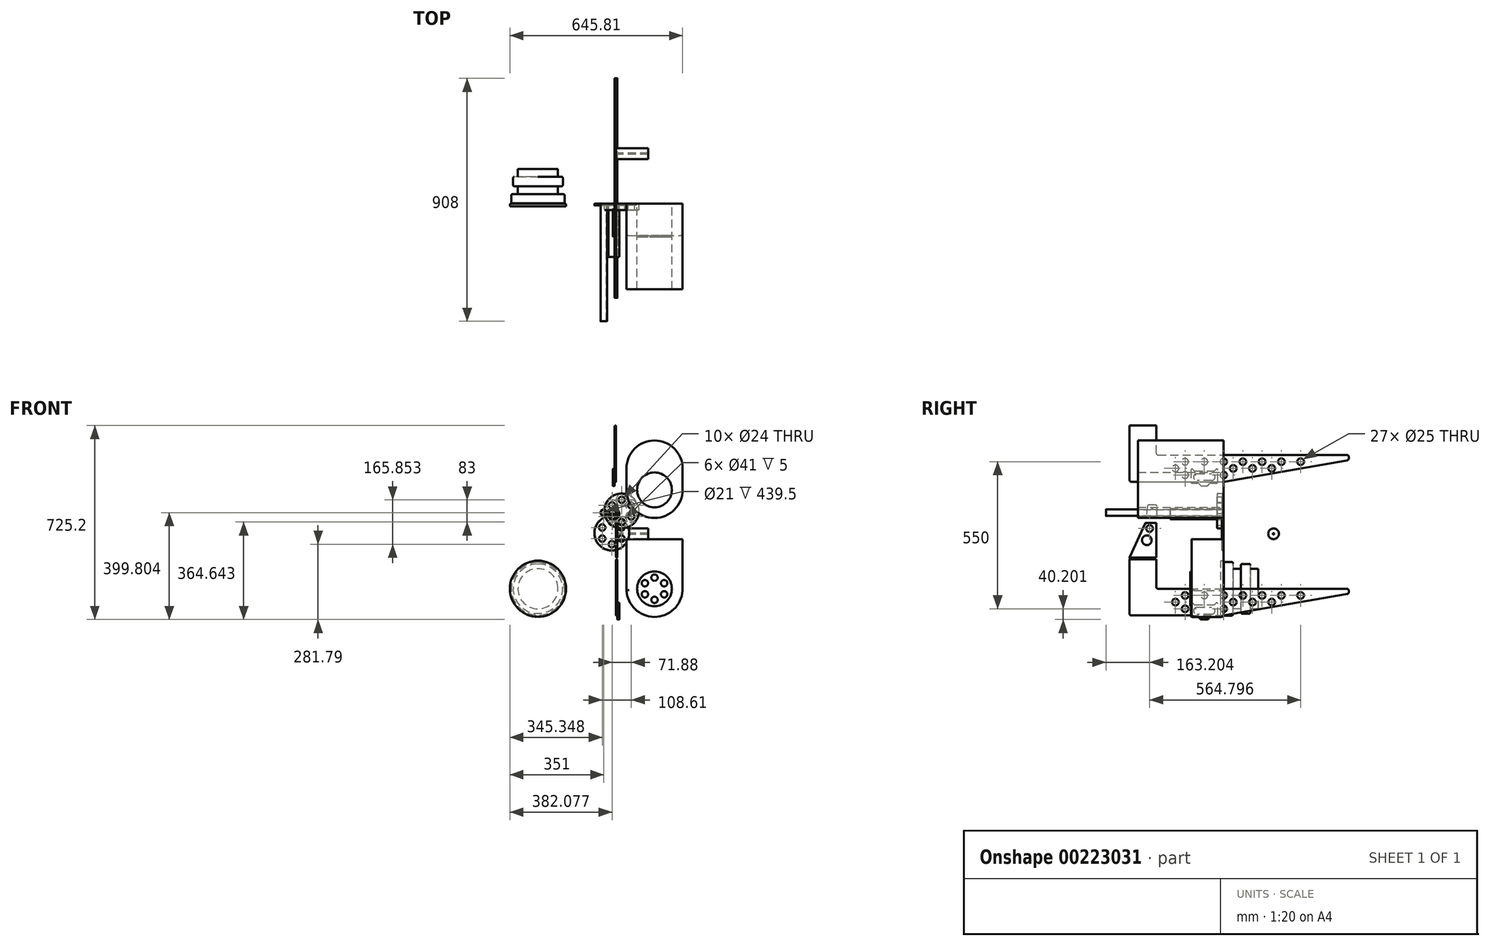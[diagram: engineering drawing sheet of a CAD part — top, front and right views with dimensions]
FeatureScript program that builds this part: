
annotation { "Feature Type Name" : "Feature", "Feature Type Description" : "" }
export const myFeature = defineFeature(function(context is Context, id is Id, definition is map)
    precondition{}
    {
        {
            var Q0;
            Q0=qCreatedBy(makeId("Front.planeOp"),FACE);
            var sketch = newSketch(context, id + "F0", { "sketchPlane" : qUnion([Q0])});
            skCircle(sketch, "E0", {"center": v(-46.15, 24.2) * mm, "radius": 10.5 * mm});
            skCircle(sketch, "E1", {"center": v(-46.15, 24.2) * mm, "radius": 12 * mm});
            skSolve(sketch);
        }
        {
            assignVariable(context, id + "F1", {"name" : "frontbarrel", "anyValue" : 440});
        }
        {
            var Q0;
            Q0=makeQuery(id+"F0.imprint","IMPRINT",FACE,{"disambiguationData":[TD([[makeQuery(id+"F0.imprint","IMPRINT",EDGE,{"derivedFrom":sQuery(id+"F0.wireOp",EDGE,"E0")}),-1.0]])]});
            extrude(context, id + "F2", {"entities" : qUnion([Q0]), "depth" : (getVariable(context, 'frontbarrel')) * mm});
        }
        {
            var Q0;
            Q0=qCreatedBy(makeId("Front.planeOp"),FACE);
            var sketch = newSketch(context, id + "F3", { "sketchPlane" : qUnion([Q0])});
            skCircle(sketch, "E2", {"center": v(-7.96, 19.9) * mm, "radius": 20.5 * mm});
            skCircle(sketch, "E3", {"center": v(-7.96, 19.9) * mm, "radius": 19 * mm});
            skCircle(sketch, "E4", {"center": v(-7.96, 19.9) * mm, "radius": 12 * mm, "construction": true});
            skPoint(sketch, "E5", {"position": v(-46.15, 24.2) * mm});
            skPoint(sketch, "E6", {"position": v(-46.38, 36.2) * mm});
            skCircle(sketch, "E7", {"center": v(-46.15, 24.2) * mm, "radius": 12 * mm, "construction": true});
            skSolve(sketch);
        }
        {
            var Q0;
            Q0=makeQuery(id+"F3.imprint","IMPRINT",FACE,{"disambiguationData":[TD([[makeQuery(id+"F3.imprint","IMPRINT",EDGE,{"derivedFrom":sQuery(id+"F3.wireOp",EDGE,"E2")}),1.0]])]});
            extrude(context, id + "F4", {"entities" : qUnion([Q0]), "depth" : 200 * mm});
        }
        {
            var Q0;
            Q0=qCreatedBy(makeId("Front.planeOp"),FACE);
            var sketch = newSketch(context, id + "F5", { "sketchPlane" : qUnion([Q0])});
            skPoint(sketch, "E8", {"position": v(-7.96, 19.9) * mm});
            skPoint(sketch, "E9", {"position": v(-24.67, 31.78) * mm});
            skPoint(sketch, "E10", {"position": v(-46.15, 24.2) * mm});
            skPoint(sketch, "E11", {"position": v(-43.79, 35.97) * mm});
            skCircle(sketch, "E12", {"center": v(-7.96, 19.9) * mm, "radius": 20.5 * mm, "construction": true});
            skCircle(sketch, "E13", {"center": v(-46.15, 24.2) * mm, "radius": 12 * mm, "construction": true});
            skCircle(sketch, "E14", {"center": v(-15.86, -52.31) * mm, "radius": 65 * mm});
            skCircle(sketch, "E15", {"center": v(-15.86, -52.31) * mm, "radius": 62 * mm, "construction": true});
            skPoint(sketch, "E16", {"position": v(-15.86, 9.69) * mm});
            skCircle(sketch, "E17", {"center": v(-15.86, -10.81) * mm, "radius": 20.5 * mm, "construction": true});
            skCircle(sketch, "E18.1.0", {"center": v(-51.8, -31.56) * mm, "radius": 20.5 * mm, "construction": true});
            skCircle(sketch, "E18.2.0", {"center": v(-51.8, -73.06) * mm, "radius": 20.5 * mm, "construction": true});
            skCircle(sketch, "E18.3.0", {"center": v(-15.86, -93.81) * mm, "radius": 20.5 * mm, "construction": true});
            skCircle(sketch, "E18.4.0", {"center": v(20.08, -73.06) * mm, "radius": 20.5 * mm, "construction": true});
            skCircle(sketch, "E18.5.0", {"center": v(20.08, -31.56) * mm, "radius": 20.5 * mm, "construction": true});
            skCircle(sketch, "E19", {"center": v(-15.86, -10.81) * mm, "radius": 12 * mm});
            skCircle(sketch, "E20.1.0", {"center": v(-51.8, -31.56) * mm, "radius": 12 * mm});
            skCircle(sketch, "E20.2.0", {"center": v(-51.8, -73.06) * mm, "radius": 12 * mm});
            skCircle(sketch, "E20.3.0", {"center": v(-15.86, -93.81) * mm, "radius": 12 * mm});
            skCircle(sketch, "E20.4.0", {"center": v(20.08, -73.06) * mm, "radius": 12 * mm});
            skCircle(sketch, "E20.5.0", {"center": v(20.08, -31.56) * mm, "radius": 12 * mm});
            skSolve(sketch);
        }
        {
            var Q0;
            Q0=makeQuery(id+"F5.imprint","IMPRINT",FACE,{"disambiguationData":[TD([[makeQuery(id+"F5.imprint","IMPRINT",EDGE,{"derivedFrom":sQuery(id+"F5.wireOp",EDGE,"E14")}),1.0]])]});
            extrude(context, id + "F6", {"entities" : qUnion([Q0]), "depth" : 7 * mm});
        }
        {
            var Q0;
            Q0=qCreatedBy(makeId("Front.planeOp"),FACE);
            var sketch = newSketch(context, id + "F7", { "sketchPlane" : qUnion([Q0])});
            skCircle(sketch, "E21", {"center": v(20.87, 30.54) * mm, "radius": 65 * mm});
            skPoint(sketch, "E22", {"position": v(-15.86, -52.31) * mm});
            skPoint(sketch, "E23", {"position": v(27.16, -3.59) * mm});
            skCircle(sketch, "E24", {"center": v(-15.86, -52.31) * mm, "radius": 65 * mm, "construction": true});
            skPoint(sketch, "E25", {"position": v(20.87, 95.54) * mm});
            skPoint(sketch, "E26", {"position": v(-15.86, -93.81) * mm});
            skLineSegment(sketch, "E27", {"start": v(-15.86, -93.81) * mm, "end": v(-15.86, -52.31) * mm, "construction": true});
            skLineSegment(sketch, "E28", {"start": v(20.87, 30.54) * mm, "end": v(20.87, 72.04) * mm, "construction": true});
            skPoint(sketch, "E29", {"position": v(-7.96, 40.4) * mm});
            skPoint(sketch, "E30", {"position": v(-7.96, 19.9) * mm});
            skCircle(sketch, "E31", {"center": v(-7.96, 19.9) * mm, "radius": 20.5 * mm, "construction": true});
            skPoint(sketch, "E32", {"position": v(-46.15, 24.2) * mm});
            skPoint(sketch, "E33", {"position": v(-46.15, 36.2) * mm});
            skCircle(sketch, "E34", {"center": v(-46.15, 24.2) * mm, "radius": 12 * mm, "construction": true});
            skCircle(sketch, "E35", {"center": v(20.87, 72.04) * mm, "radius": 12 * mm});
            skCircle(sketch, "E36.1.0", {"center": v(-15.07, 51.3) * mm, "radius": 12 * mm});
            skCircle(sketch, "E36.2.0", {"center": v(-15.07, 9.8) * mm, "radius": 12 * mm});
            skCircle(sketch, "E36.3.0", {"center": v(20.87, -10.96) * mm, "radius": 12 * mm});
            skCircle(sketch, "E36.4.0", {"center": v(56.8, 9.8) * mm, "radius": 12 * mm});
            skCircle(sketch, "E36.5.0", {"center": v(56.8, 51.3) * mm, "radius": 12 * mm});
            skSolve(sketch);
        }
        {
            var Q0;
            Q0=makeQuery(id+"F7.imprint","IMPRINT",FACE,{"disambiguationData":[TD([[makeQuery(id+"F7.imprint","IMPRINT",EDGE,{"derivedFrom":sQuery(id+"F7.wireOp",EDGE,"E21")}),1.0]])]});
            extrude(context, id + "F8", {"entities" : qUnion([Q0]), "depth" : 24 * mm});
        }
        {
            var Q0;
            Q0=makeQuery(id+"F8.opExtrude","CAP_FACE",FACE,{"disambiguationData":[OSD([sQuery(id+"F7.wireOp",EDGE,"E21"),sQuery(id+"F7.wireOp",EDGE,"E35"),sQuery(id+"F7.wireOp",EDGE,"E36.1.0"),sQuery(id+"F7.wireOp",EDGE,"E36.2.0"),sQuery(id+"F7.wireOp",EDGE,"E36.3.0"),sQuery(id+"F7.wireOp",EDGE,"E36.4.0"),sQuery(id+"F7.wireOp",EDGE,"E36.5.0")])],"isStart":true});
            var sketch = newSketch(context, id + "F9", { "sketchPlane" : qUnion([Q0])});
            skPoint(sketch, "E37", {"position": v(-20.87, 72.04) * mm});
            skPoint(sketch, "E38", {"position": v(7.96, 19.9) * mm});
            skPoint(sketch, "E39", {"position": v(7.96, 40.4) * mm});
            skCircle(sketch, "E40", {"center": v(7.96, 19.9) * mm, "radius": 20.5 * mm, "construction": true});
            skCircle(sketch, "E41", {"center": v(-20.87, 72.04) * mm, "radius": 20.5 * mm});
            skPoint(sketch, "E42", {"position": v(-20.87, 30.54) * mm});
            skPoint(sketch, "E43", {"position": v(-23.92, 92.31) * mm});
            skCircle(sketch, "E44.1.0", {"center": v(-56.8, 51.3) * mm, "radius": 20.5 * mm});
            skCircle(sketch, "E44.2.0", {"center": v(-56.8, 9.8) * mm, "radius": 20.5 * mm});
            skCircle(sketch, "E44.3.0", {"center": v(-20.87, -10.96) * mm, "radius": 20.5 * mm});
            skCircle(sketch, "E44.4.0", {"center": v(15.07, 9.8) * mm, "radius": 20.5 * mm});
            skCircle(sketch, "E44.5.0", {"center": v(15.07, 51.3) * mm, "radius": 20.5 * mm});
            skSolve(sketch);
        }
        {
            var Q0;
            Q0=makeQuery(id+"F9.imprint","IMPRINT",FACE,{"disambiguationData":[TD([[makeQuery(id+"F9.imprint","IMPRINT",EDGE,{"derivedFrom":sQuery(id+"F9.wireOp",EDGE,"E41")}),1.0]])]});
            var Q1;
            Q1=makeQuery(id+"F9.imprint","IMPRINT",FACE,{"disambiguationData":[TD([[makeQuery(id+"F9.imprint","IMPRINT",EDGE,{"derivedFrom":sQuery(id+"F9.wireOp",EDGE,"E44.1.0")}),1.0]])]});
            var Q2;
            Q2=makeQuery(id+"F9.imprint","IMPRINT",FACE,{"disambiguationData":[TD([[makeQuery(id+"F9.imprint","IMPRINT",EDGE,{"derivedFrom":sQuery(id+"F9.wireOp",EDGE,"E44.2.0")}),1.0]])]});
            var Q3;
            Q3=makeQuery(id+"F9.imprint","IMPRINT",FACE,{"disambiguationData":[TD([[makeQuery(id+"F9.imprint","IMPRINT",EDGE,{"derivedFrom":sQuery(id+"F9.wireOp",EDGE,"E44.3.0")}),1.0]])]});
            var Q4;
            Q4=makeQuery(id+"F9.imprint","IMPRINT",FACE,{"disambiguationData":[TD([[makeQuery(id+"F9.imprint","IMPRINT",EDGE,{"derivedFrom":sQuery(id+"F9.wireOp",EDGE,"E44.4.0")}),1.0]])]});
            var Q5;
            Q5=makeQuery(id+"F9.imprint","IMPRINT",FACE,{"disambiguationData":[TD([[makeQuery(id+"F9.imprint","IMPRINT",EDGE,{"derivedFrom":sQuery(id+"F9.wireOp",EDGE,"E44.5.0")}),1.0]])]});
            extrude(context, id + "F10", {"entities" : qUnion([Q0, Q1, Q2, Q3, Q4, Q5]), "operationType" : NewBodyOperationType.REMOVE, "oppositeDirection" : true, "depth" : 5 * mm});
        }
        {
            var Q0;
            Q0=makeQuery(id+"F2.opExtrude","CAP_EDGE",EDGE,{"disambiguationData":[OSD([sQuery(id+"F0.wireOp",EDGE,"E1")])],"isStart":false});
            fillet(context, id + "F11", {"entities" : qUnion([Q0]), "radius" : 0.5 * mm, "tangentPropagation" : true, "allowEdgeOverflow" : false});
        }
        {
            var Q0;
            Q0=makeQuery(id+"F2.opExtrude","CAP_EDGE",EDGE,{"disambiguationData":[OSD([sQuery(id+"F0.wireOp",EDGE,"E0")])],"isStart":false});
            fillet(context, id + "F12", {"entities" : qUnion([Q0]), "radius" : 0.5 * mm, "tangentPropagation" : true, "allowEdgeOverflow" : false});
        }
        {
            var Q0;
            Q0=makeQuery(id+"F6.opExtrude","CAP_FACE",FACE,{"disambiguationData":[OSD([sQuery(id+"F5.wireOp",EDGE,"E14"),sQuery(id+"F5.wireOp",EDGE,"E19"),sQuery(id+"F5.wireOp",EDGE,"E20.1.0"),sQuery(id+"F5.wireOp",EDGE,"E20.2.0"),sQuery(id+"F5.wireOp",EDGE,"E20.3.0"),sQuery(id+"F5.wireOp",EDGE,"E20.4.0"),sQuery(id+"F5.wireOp",EDGE,"E20.5.0")])],"isStart":false});
            var Q1;
            Q1=makeQuery(id+"F6.opExtrude","CAP_EDGE",EDGE,{"disambiguationData":[OSD([sQuery(id+"F5.wireOp",EDGE,"E14")])],"isStart":true});
            fillet(context, id + "F13", {"entities" : qUnion([Q0, Q1]), "radius" : 1 * mm, "tangentPropagation" : true, "allowEdgeOverflow" : false});
        }
        {
            var Q0;
            Q0=makeQuery(id+"F8.opExtrude","CAP_EDGE",EDGE,{"disambiguationData":[OSD([sQuery(id+"F7.wireOp",EDGE,"E21")])],"isStart":false});
            var Q1;
            Q1=makeQuery(id+"F8.opExtrude","CAP_EDGE",EDGE,{"disambiguationData":[OSD([sQuery(id+"F7.wireOp",EDGE,"E21")])],"isStart":true});
            fillet(context, id + "F14", {"entities" : qUnion([Q0, Q1]), "radius" : 2 * mm, "tangentPropagation" : true, "allowEdgeOverflow" : false});
        }
        {
            var Q0;
            Q0=qCreatedBy(makeId("Right.planeOp"),FACE);
            var sketch = newSketch(context, id + "F15", { "sketchPlane" : qUnion([Q0])});
            skLineSegment(sketch, "E45", {"start": v(-245, -260.4) * mm, "end": v(461, -260.4) * mm, "construction": true});
            skLineSegment(sketch, "E46", {"start": v(-252, -260.4) * mm, "end": v(468, -260.4) * mm});
            skLineSegment(sketch, "E47", {"start": v(-345, -360.4) * mm, "end": v(-0.6, -360.4) * mm});
            skLineSegment(sketch, "E48", {"start": v(-252, -253.4) * mm, "end": v(-252, -150.4) * mm});
            skLineSegment(sketch, "E49", {"start": v(-252, -150.4) * mm, "end": v(-352, -150.4) * mm});
            skLineSegment(sketch, "E50", {"start": v(-352, -150.4) * mm, "end": v(-352, -360.4) * mm});
            skLineSegment(sketch, "E51", {"start": v(-352, -310.4) * mm, "end": v(239.6, -310.4) * mm, "construction": true});
            skLineSegment(sketch, "E52", {"start": v(-352, -260.4) * mm, "end": v(-352, -353.4) * mm, "construction": true});
            skCircle(sketch, "E53", {"center": v(-180, -310.4) * mm, "radius": 12.5 * mm});
            skCircle(sketch, "E54", {"center": v(-144, -285.4) * mm, "radius": 12.5 * mm});
            skCircle(sketch, "E55", {"center": v(-144, -335.4) * mm, "radius": 12.5 * mm});
            skCircle(sketch, "E56", {"center": v(-72, -285.4) * mm, "radius": 12.5 * mm});
            skCircle(sketch, "E57", {"center": v(0, -285.4) * mm, "radius": 12.5 * mm});
            skCircle(sketch, "E58", {"center": v(0, -335.4) * mm, "radius": 12.5 * mm});
            skCircle(sketch, "E59", {"center": v(36, -310.4) * mm, "radius": 12.5 * mm});
            skCircle(sketch, "E60", {"center": v(72, -285.4) * mm, "radius": 12.5 * mm});
            skCircle(sketch, "E61", {"center": v(108, -310.4) * mm, "radius": 12.5 * mm});
            skCircle(sketch, "E62", {"center": v(144, -285.4) * mm, "radius": 12.5 * mm});
            skCircle(sketch, "E63", {"center": v(216, -285.4) * mm, "radius": 12.5 * mm});
            skCircle(sketch, "E64", {"center": v(180, -310.4) * mm, "radius": 12.5 * mm});
            skCircle(sketch, "E65", {"center": v(288, -285.4) * mm, "radius": 12.5 * mm});
            skLineSegment(sketch, "E66", {"start": v(-72, -380.4) * mm, "end": v(-36, -380.4) * mm, "construction": true});
            skLineSegment(sketch, "E67", {"start": v(-36, -400.4) * mm, "end": v(0, -400.4) * mm, "construction": true});
            skLineSegment(sketch, "E68", {"start": v(0, -380.4) * mm, "end": v(36, -380.4) * mm, "construction": true});
            skLineSegment(sketch, "E69", {"start": v(36, -400.4) * mm, "end": v(72, -400.4) * mm, "construction": true});
            skLineSegment(sketch, "E70", {"start": v(72, -380.4) * mm, "end": v(108, -380.4) * mm, "construction": true});
            skLineSegment(sketch, "E71", {"start": v(108, -400.4) * mm, "end": v(144, -400.4) * mm, "construction": true});
            skLineSegment(sketch, "E72", {"start": v(144, -380.4) * mm, "end": v(180, -380.4) * mm, "construction": true});
            skLineSegment(sketch, "E73", {"start": v(180, -400.4) * mm, "end": v(216, -400.4) * mm, "construction": true});
            skLineSegment(sketch, "E74", {"start": v(-252, -260.4) * mm, "end": v(-252, -310.4) * mm, "construction": true});
            skLineSegment(sketch, "E75", {"start": v(-252, -310.4) * mm, "end": v(-252, -360.4) * mm, "construction": true});
            skPoint(sketch, "E76", {"position": v(-252, -285.4) * mm});
            skPoint(sketch, "E77", {"position": v(-252, -335.4) * mm});
            skLineSegment(sketch, "E78", {"start": v(-72, -400.4) * mm, "end": v(-108, -400.4) * mm, "construction": true});
            skLineSegment(sketch, "E79", {"start": v(-108, -380.4) * mm, "end": v(-144, -380.4) * mm, "construction": true});
            skLineSegment(sketch, "E80", {"start": v(-144, -400.4) * mm, "end": v(-180, -400.4) * mm, "construction": true});
            skLineSegment(sketch, "E81", {"start": v(216, -380.4) * mm, "end": v(252, -380.4) * mm, "construction": true});
            skLineSegment(sketch, "E82", {"start": v(252, -400.4) * mm, "end": v(288, -400.4) * mm, "construction": true});
            skLineSegment(sketch, "E83", {"start": v(-144, -335.4) * mm, "end": v(-144, -360.4) * mm, "construction": true});
            skLineSegment(sketch, "E84", {"start": v(-180, -310.4) * mm, "end": v(-180, -297.9) * mm, "construction": true});
            skLineSegment(sketch, "E85", {"start": v(468, -267.4) * mm, "end": v(468, -273.26) * mm});
            skLineSegment(sketch, "E86", {"start": v(462.2, -280.16) * mm, "end": v(0.6, -360.3) * mm});
            skLineSegment(sketch, "E87", {"start": v(288, -260.4) * mm, "end": v(288, -310.4) * mm, "construction": true});
            skPoint(sketch, "E88.visualSharp", {"position": v(468, -279.15) * mm});
            skArc(sketch, "E88.filletArc", {"start": v(462.2, -280.16) * mm, "mid": v(466.36, -277.77) * mm, "end": v(468, -273.26) * mm});
            skPoint(sketch, "E89.visualSharp", {"position": v(468, -260.4) * mm});
            skArc(sketch, "E89.filletArc", {"start": v(468, -267.4) * mm, "mid": v(465.95, -262.45) * mm, "end": v(461, -260.4) * mm});
            skPoint(sketch, "E90.visualSharp", {"position": v(0, -360.4) * mm});
            skArc(sketch, "E90.filletArc", {"start": v(-0.6, -360.4) * mm, "mid": v(0, -360.37) * mm, "end": v(0.6, -360.3) * mm});
            skLineSegment(sketch, "E91", {"start": v(-144, -272.9) * mm, "end": v(-144, -260.4) * mm, "construction": true});
            skPoint(sketch, "E92.visualSharp", {"position": v(-352, -360.4) * mm});
            skArc(sketch, "E92.filletArc", {"start": v(-352, -353.4) * mm, "mid": v(-349.95, -358.35) * mm, "end": v(-345, -360.4) * mm});
            skPoint(sketch, "E93.newPointB", {"position": v(-352, -260.4) * mm});
            skArc(sketch, "E93.filletArc", {"start": v(-252, -253.4) * mm, "mid": v(-249.95, -258.35) * mm, "end": v(-245, -260.4) * mm});
            skSolve(sketch);
        }
        {
            var Q0;
            Q0=makeQuery(id+"F15.imprint","IMPRINT",FACE,{"disambiguationData":[TD([[makeQuery(id+"F15.imprint","IMPRINT",EDGE,{"derivedFrom":sQuery(id+"F15.wireOp",EDGE,"E47")}),1.0]])]});
            extrude(context, id + "F16", {"entities" : qUnion([Q0]), "depth" : 5 * mm});
        }
        {
            var Q0;
            Q0=makeQuery(id+"F16.opExtrude","CAP_FACE",FACE,{"disambiguationData":[OSD([sQuery(id+"F15.wireOp",EDGE,"E46"),sQuery(id+"F15.wireOp",EDGE,"E47"),sQuery(id+"F15.wireOp",EDGE,"E48"),sQuery(id+"F15.wireOp",EDGE,"E49"),sQuery(id+"F15.wireOp",EDGE,"E50"),sQuery(id+"F15.wireOp",EDGE,"E53"),sQuery(id+"F15.wireOp",EDGE,"E54"),sQuery(id+"F15.wireOp",EDGE,"E55"),sQuery(id+"F15.wireOp",EDGE,"E56"),sQuery(id+"F15.wireOp",EDGE,"E57"),sQuery(id+"F15.wireOp",EDGE,"E58"),sQuery(id+"F15.wireOp",EDGE,"E59"),sQuery(id+"F15.wireOp",EDGE,"E60"),sQuery(id+"F15.wireOp",EDGE,"E61"),sQuery(id+"F15.wireOp",EDGE,"E62"),sQuery(id+"F15.wireOp",EDGE,"E63"),sQuery(id+"F15.wireOp",EDGE,"E64"),sQuery(id+"F15.wireOp",EDGE,"E65"),sQuery(id+"F15.wireOp",EDGE,"E85"),sQuery(id+"F15.wireOp",EDGE,"E86"),sQuery(id+"F15.wireOp",EDGE,"E88.filletArc"),sQuery(id+"F15.wireOp",EDGE,"E89.filletArc"),sQuery(id+"F15.wireOp",EDGE,"E90.filletArc"),sQuery(id+"F15.wireOp",EDGE,"E92.filletArc"),sQuery(id+"F15.wireOp",EDGE,"E93.filletArc")])],"isStart":false});
            var sketch = newSketch(context, id + "F17", { "sketchPlane" : qUnion([Q0])});
            skPoint(sketch, "E94", {"position": v(-352, -360.4) * mm});
            skPoint(sketch, "E95", {"position": v(0.6, -360.3) * mm});
            skPoint(sketch, "E96", {"position": v(-72, -285.4) * mm});
            skPoint(sketch, "E97", {"position": v(-144, -335.4) * mm});
            skPoint(sketch, "E98", {"position": v(0, -335.4) * mm});
            skArc(sketch, "E99", {"start": v(-99.47, -329.9) * mm, "mid": v(-112.32, -342.74) * mm, "end": v(-99.47, -355.6) * mm});
            skArc(sketch, "E100", {"start": v(-44.53, -355.6) * mm, "mid": v(-31.68, -342.74) * mm, "end": v(-44.53, -329.9) * mm});
            skLineSegment(sketch, "E101", {"start": v(-99.47, -329.9) * mm, "end": v(-44.53, -329.9) * mm});
            skLineSegment(sketch, "E102", {"start": v(-44.53, -355.6) * mm, "end": v(-99.47, -355.6) * mm});
            skLineSegment(sketch, "E103", {"start": v(-122.32, -316.93) * mm, "end": v(-122.32, -361.6) * mm});
            skLineSegment(sketch, "E104", {"start": v(-118.32, -365.6) * mm, "end": v(-97.4, -365.6) * mm});
            skLineSegment(sketch, "E105", {"start": v(-92.45, -367.65) * mm, "end": v(-86.55, -373.55) * mm});
            skLineSegment(sketch, "E106", {"start": v(-81.6, -375.6) * mm, "end": v(-62.4, -375.6) * mm});
            skLineSegment(sketch, "E107", {"start": v(-57.45, -373.55) * mm, "end": v(-51.55, -367.65) * mm});
            skLineSegment(sketch, "E108", {"start": v(-46.6, -365.6) * mm, "end": v(-25.68, -365.6) * mm});
            skLineSegment(sketch, "E109", {"start": v(-21.68, -361.6) * mm, "end": v(-21.68, -316.93) * mm});
            skLineSegment(sketch, "E110", {"start": v(-99.47, -342.74) * mm, "end": v(-122.32, -342.74) * mm, "construction": true});
            skPoint(sketch, "E110.endSnap0", {"position": v(-112.32, -342.74) * mm});
            skLineSegment(sketch, "E111", {"start": v(-44.53, -342.74) * mm, "end": v(-21.68, -342.74) * mm, "construction": true});
            skLineSegment(sketch, "E112", {"start": v(-94.5, -365.6) * mm, "end": v(-49.5, -365.6) * mm, "construction": true});
            skPoint(sketch, "E113", {"position": v(-72, -375.6) * mm});
            skPoint(sketch, "E114", {"position": v(-72, -365.6) * mm});
            skPoint(sketch, "E115.visualSharp", {"position": v(-94.5, -365.6) * mm});
            skArc(sketch, "E115.filletArc", {"start": v(-92.45, -367.65) * mm, "mid": v(-94.72, -366.13) * mm, "end": v(-97.4, -365.6) * mm});
            skPoint(sketch, "E116.visualSharp", {"position": v(-84.5, -375.6) * mm});
            skArc(sketch, "E116.filletArc", {"start": v(-86.55, -373.55) * mm, "mid": v(-84.28, -375.06) * mm, "end": v(-81.6, -375.6) * mm});
            skPoint(sketch, "E117.visualSharp", {"position": v(-59.5, -375.6) * mm});
            skArc(sketch, "E117.filletArc", {"start": v(-62.4, -375.6) * mm, "mid": v(-59.72, -375.06) * mm, "end": v(-57.45, -373.55) * mm});
            skPoint(sketch, "E118.visualSharp", {"position": v(-49.5, -365.6) * mm});
            skArc(sketch, "E118.filletArc", {"start": v(-46.6, -365.6) * mm, "mid": v(-49.28, -366.13) * mm, "end": v(-51.55, -367.65) * mm});
            skLineSegment(sketch, "E119", {"start": v(-99.47, -342.74) * mm, "end": v(-44.53, -342.74) * mm, "construction": true});
            skPoint(sketch, "E120", {"position": v(-72, -342.74) * mm});
            skLineSegment(sketch, "E121", {"start": v(-108.22, -319.9) * mm, "end": v(-35.78, -319.9) * mm});
            skLineSegment(sketch, "E122", {"start": v(-109.92, -319.9) * mm, "end": v(-122.32, -319.9) * mm, "construction": true});
            skLineSegment(sketch, "E123", {"start": v(-34.08, -319.9) * mm, "end": v(-21.68, -319.9) * mm, "construction": true});
            skLineSegment(sketch, "E124", {"start": v(-118.32, -312.93) * mm, "end": v(-118.1, -312.93) * mm});
            skLineSegment(sketch, "E125", {"start": v(-25.68, -312.93) * mm, "end": v(-25.68, -312.93) * mm});
            skPoint(sketch, "E126", {"position": v(-72, -319.9) * mm});
            skLineSegment(sketch, "E127", {"start": v(-111.1, -318.66) * mm, "end": v(-115.44, -314.16) * mm});
            skLineSegment(sketch, "E128", {"start": v(-32.9, -318.66) * mm, "end": v(-28.56, -314.16) * mm});
            skPoint(sketch, "E129.visualSharp", {"position": v(-122.32, -312.93) * mm});
            skArc(sketch, "E129.filletArc", {"start": v(-119.22, -313.03) * mm, "mid": v(-121.45, -314.44) * mm, "end": v(-122.32, -316.93) * mm});
            skPoint(sketch, "E130.visualSharp", {"position": v(-109.92, -319.9) * mm});
            skArc(sketch, "E130.filletArc", {"start": v(-111.1, -318.66) * mm, "mid": v(-109.79, -319.57) * mm, "end": v(-108.22, -319.9) * mm});
            skArc(sketch, "E131.filletArc", {"start": v(-115.44, -314.16) * mm, "mid": v(-117.18, -313.1) * mm, "end": v(-119.22, -313.03) * mm});
            skPoint(sketch, "E132.visualSharp", {"position": v(-21.68, -312.93) * mm});
            skArc(sketch, "E132.filletArc", {"start": v(-21.68, -316.93) * mm, "mid": v(-22.85, -314.1) * mm, "end": v(-25.68, -312.93) * mm});
            skPoint(sketch, "E133.visualSharp", {"position": v(-27.38, -312.93) * mm});
            skArc(sketch, "E133.filletArc", {"start": v(-25.68, -312.93) * mm, "mid": v(-27.25, -313.25) * mm, "end": v(-28.56, -314.16) * mm});
            skPoint(sketch, "E134.visualSharp", {"position": v(-34.08, -319.9) * mm});
            skArc(sketch, "E134.filletArc", {"start": v(-35.78, -319.9) * mm, "mid": v(-34.21, -319.57) * mm, "end": v(-32.9, -318.66) * mm});
            skPoint(sketch, "E135.visualSharp", {"position": v(-21.68, -365.6) * mm});
            skArc(sketch, "E135.filletArc", {"start": v(-25.68, -365.6) * mm, "mid": v(-22.85, -364.43) * mm, "end": v(-21.68, -361.6) * mm});
            skPoint(sketch, "E136.visualSharp", {"position": v(-122.32, -365.6) * mm});
            skArc(sketch, "E136.filletArc", {"start": v(-122.32, -361.6) * mm, "mid": v(-121.15, -364.43) * mm, "end": v(-118.32, -365.6) * mm});
            skLineSegment(sketch, "E137", {"start": v(-129.6, -319.9) * mm, "end": v(-129.6, -365.6) * mm, "construction": true});
            skPoint(sketch, "E138", {"position": v(-129.6, -342.74) * mm});
            skLineSegment(sketch, "E139", {"start": v(-72, -365.6) * mm, "end": v(-72, -355.6) * mm, "construction": true});
            skLineSegment(sketch, "E140", {"start": v(-72, -365.6) * mm, "end": v(-72, -375.6) * mm, "construction": true});
            skLineSegment(sketch, "E141", {"start": v(-122.32, -327.75) * mm, "end": v(-112.32, -327.75) * mm, "construction": true});
            skSolve(sketch);
        }
        {
            var Q0;
            Q0 = qSketchRegion(id + "F17", true);
            extrude(context, id + "F18", {"entities" : qUnion([Q0]), "operationType" : NewBodyOperationType.ADD, "depth" : 7 * mm});
        }
        {
            var Q0;
            Q0=qCreatedBy(makeId("Right.planeOp"),FACE);
            var sketch = newSketch(context, id + "F19", { "sketchPlane" : qUnion([Q0])});
            skPoint(sketch, "E142", {"position": v(-352, -150.4) * mm});
            skPoint(sketch, "E143", {"position": v(-252, -150.4) * mm});
            skLineSegment(sketch, "E144", {"start": v(-352, -144.04) * mm, "end": v(-252, -144.04) * mm});
            skLineSegment(sketch, "E145", {"start": v(-252, -144.04) * mm, "end": v(-252, -14.04) * mm});
            skLineSegment(sketch, "E146", {"start": v(-252, -14.04) * mm, "end": v(-291.75, -14.04) * mm});
            skLineSegment(sketch, "E147", {"start": v(-291.75, -14.04) * mm, "end": v(-352, -144.04) * mm});
            skPoint(sketch, "E148", {"position": v(-271.87, -14.04) * mm});
            skPoint(sketch, "E149", {"position": v(-302, -144.04) * mm});
            skLineSegment(sketch, "E150", {"start": v(-271.87, -14.04) * mm, "end": v(-302, -144.04) * mm, "construction": true});
            skCircle(sketch, "E151", {"center": v(-286.91, -78.94) * mm, "radius": 18.2 * mm});
            skCircle(sketch, "E152", {"center": v(-276.8, -35.28) * mm, "radius": 12.5 * mm});
            skSolve(sketch);
        }
        {
            var Q0;
            Q0=makeQuery(id+"F19.imprint","IMPRINT",FACE,{"disambiguationData":[TD([[makeQuery(id+"F19.imprint","IMPRINT",EDGE,{"derivedFrom":sQuery(id+"F19.wireOp",EDGE,"E144")}),1.0]])]});
            extrude(context, id + "F20", {"entities" : qUnion([Q0]), "depth" : 5 * mm});
        }
        {
            var Q0;
            Q0=makeQuery(id+"F16.opExtrude","CAP_EDGE",EDGE,{"disambiguationData":[OSD([sQuery(id+"F15.wireOp",EDGE,"E49")])],"isStart":true});
            var Q1;
            Q1=makeQuery(id+"F16.opExtrude","CAP_EDGE",EDGE,{"disambiguationData":[OSD([sQuery(id+"F15.wireOp",EDGE,"E49")])],"isStart":false});
            var Q2;
            Q2=makeQuery(id+"F20.opExtrude","CAP_EDGE",EDGE,{"disambiguationData":[OSD([sQuery(id+"F19.wireOp",EDGE,"E144")])],"isStart":true});
            var Q3;
            Q3=makeQuery(id+"F20.opExtrude","CAP_EDGE",EDGE,{"disambiguationData":[OSD([sQuery(id+"F19.wireOp",EDGE,"E144")])],"isStart":false});
            var Q4;
            Q4=makeQuery(id+"F20.opExtrude","CAP_EDGE",EDGE,{"disambiguationData":[OSD([sQuery(id+"F19.wireOp",EDGE,"E146")])],"isStart":true});
            var Q5;
            Q5=makeQuery(id+"F20.opExtrude","CAP_EDGE",EDGE,{"disambiguationData":[OSD([sQuery(id+"F19.wireOp",EDGE,"E146")])],"isStart":false});
            fillet(context, id + "F21", {"entities" : qUnion([Q0, Q1, Q2, Q3, Q4, Q5]), "radius" : 2.5 * mm, "tangentPropagation" : true, "allowEdgeOverflow" : false});
        }
        {
            var Q0;
            Q0=qCreatedBy(makeId("Right.planeOp"),FACE);
            var sketch = newSketch(context, id + "F22", { "sketchPlane" : qUnion([Q0])});
            skPoint(sketch, "E153", {"position": v(-291.75, -14.04) * mm});
            skPoint(sketch, "E154", {"position": v(-352, -144.04) * mm});
            skPoint(sketch, "E155", {"position": v(-252, -14.04) * mm});
            skLineSegment(sketch, "E156", {"start": v(-288.75, 13.18) * mm, "end": v(-284.9, 48.18) * mm, "construction": true});
            skLineSegment(sketch, "E157", {"start": v(-252, -14.04) * mm, "end": v(-291.75, -14.04) * mm, "construction": true});
            skLineSegment(sketch, "E158", {"start": v(-249.04, 7.63) * mm, "end": v(-249.04, 47.63) * mm});
            skLineSegment(sketch, "E159", {"start": v(-254.04, 52.63) * mm, "end": v(-279.94, 52.63) * mm});
            skLineSegment(sketch, "E160", {"start": v(-284.9, 48.18) * mm, "end": v(-288.75, 13.18) * mm});
            skArc(sketch, "E161.filletArc", {"start": v(-279.94, 52.63) * mm, "mid": v(-283.27, 51.36) * mm, "end": v(-284.9, 48.18) * mm});
            skPoint(sketch, "E162.visualSharp", {"position": v(-249.04, 52.63) * mm});
            skArc(sketch, "E162.filletArc", {"start": v(-249.04, 47.63) * mm, "mid": v(-250.5, 51.17) * mm, "end": v(-254.04, 52.63) * mm});
            skLineSegment(sketch, "E163", {"start": v(-288.78, 12.63) * mm, "end": v(-288.78, 7.63) * mm});
            skLineSegment(sketch, "E164", {"start": v(-288.78, 7.63) * mm, "end": v(-249.04, 7.63) * mm});
            skArc(sketch, "E165.filletArc", {"start": v(-288.75, 13.18) * mm, "mid": v(-288.78, 12.9) * mm, "end": v(-288.78, 12.63) * mm});
            skPoint(sketch, "E166", {"position": v(-266.99, 52.63) * mm});
            skLineSegment(sketch, "E167", {"start": v(-266.99, -5.87) * mm, "end": v(-254.04, -5.87) * mm, "construction": true});
            skLineSegment(sketch, "E168", {"start": v(-266.99, 52.63) * mm, "end": v(-266.99, 39.68) * mm, "construction": true});
            skCircle(sketch, "E169", {"center": v(-266.99, 39.68) * mm, "radius": 2.5 * mm});
            skSolve(sketch);
        }
        {
            var Q0;
            Q0=makeQuery(id+"F22.imprint","IMPRINT",FACE,{"disambiguationData":[TD([[makeQuery(id+"F22.imprint","IMPRINT",EDGE,{"derivedFrom":sQuery(id+"F22.wireOp",EDGE,"E158")}),1.0]])]});
            extrude(context, id + "F23", {"entities" : qUnion([Q0]), "depth" : 5 * mm});
        }
        {
            var Q0;
            Q0=makeQuery(id+"F23.opExtrude","CAP_EDGE",EDGE,{"disambiguationData":[OSD([sQuery(id+"F22.wireOp",EDGE,"E164")])],"isStart":false});
            var Q1;
            Q1=makeQuery(id+"F23.opExtrude","CAP_EDGE",EDGE,{"disambiguationData":[OSD([sQuery(id+"F22.wireOp",EDGE,"E164")])],"isStart":true});
            fillet(context, id + "F24", {"entities" : qUnion([Q0, Q1]), "radius" : 2.5 * mm, "tangentPropagation" : true, "allowEdgeOverflow" : false});
        }
        {
            var Q0;
            Q0=qCreatedBy(makeId("Front.planeOp"),FACE);
            var sketch = newSketch(context, id + "F25", { "sketchPlane" : qUnion([Q0])});
            skPoint(sketch, "E170", {"position": v(20.87, 30.54) * mm});
            skPoint(sketch, "E171", {"position": v(85.87, 30.54) * mm});
            skLineSegment(sketch, "E172", {"start": v(20.87, 30.54) * mm, "end": v(85.87, 30.54) * mm, "construction": true});
            skArc(sketch, "E173", {"start": v(38.66, -266.54) * mm, "mid": v(143.66, -365.64) * mm, "end": v(248.66, -266.54) * mm});
            skLineSegment(sketch, "E174", {"start": v(38.66, -266.54) * mm, "end": v(38.66, -75.46) * mm});
            skLineSegment(sketch, "E175", {"start": v(38.66, -75.46) * mm, "end": v(248.66, -75.46) * mm});
            skLineSegment(sketch, "E176", {"start": v(248.66, -75.46) * mm, "end": v(248.66, -266.54) * mm});
            skPoint(sketch, "E177", {"position": v(143.66, -75.46) * mm});
            skLineSegment(sketch, "E178", {"start": v(143.66, -12.15) * mm, "end": v(208.66, -12.15) * mm, "construction": true});
            skLineSegment(sketch, "E179", {"start": v(208.66, 12.22) * mm, "end": v(248.66, 12.22) * mm, "construction": true});
            skPoint(sketch, "E180", {"position": v(143.66, -365.64) * mm});
            skSolve(sketch);
        }
        {
            var Q0;
            Q0=makeQuery(id+"F25.imprint","IMPRINT",FACE,{"disambiguationData":[TD([[makeQuery(id+"F25.imprint","IMPRINT",EDGE,{"derivedFrom":sQuery(id+"F25.wireOp",EDGE,"E173")}),1.0]])]});
            extrude(context, id + "F26", {"entities" : qUnion([Q0]), "depth" : 120 * mm});
        }
        {
            var Q0;
            Q0=makeQuery(id+"F26.opExtrude","CAP_EDGE",EDGE,{"disambiguationData":[OSD([sQuery(id+"F25.wireOp",EDGE,"E173")])],"isStart":true});
            var Q1;
            Q1=makeQuery(id+"F26.opExtrude","CAP_EDGE",EDGE,{"disambiguationData":[OSD([sQuery(id+"F25.wireOp",EDGE,"E176")])],"isStart":true});
            var Q2;
            Q2=makeQuery(id+"F26.opExtrude","CAP_EDGE",EDGE,{"disambiguationData":[OSD([sQuery(id+"F25.wireOp",EDGE,"E176")])],"isStart":false});
            var Q3;
            Q3=makeQuery(id+"F26.opExtrude","CAP_EDGE",EDGE,{"disambiguationData":[OSD([sQuery(id+"F25.wireOp",EDGE,"E173")])],"isStart":false});
            var Q4;
            Q4=makeQuery(id+"F26.opExtrude","SWEPT_EDGE",EDGE,{"disambiguationData":[OSD([sQuery(id+"F25.wireOp",EDGE,"E173"),sQuery(id+"F25.wireOp",EDGE,"E176")])]});
            var Q5;
            Q5=makeQuery(id+"F26.opExtrude","CAP_EDGE",EDGE,{"disambiguationData":[OSD([sQuery(id+"F25.wireOp",EDGE,"E174")])],"isStart":false});
            var Q6;
            Q6=makeQuery(id+"F26.opExtrude","CAP_EDGE",EDGE,{"disambiguationData":[OSD([sQuery(id+"F25.wireOp",EDGE,"E174")])],"isStart":true});
            fillet(context, id + "F27", {"entities" : qUnion([Q0, Q1, Q2, Q3, Q4, Q5, Q6]), "radius" : 10 * mm, "tangentPropagation" : true, "allowEdgeOverflow" : false});
        }
        {
            var Q0;
            Q0=makeQuery(id+"F16.opExtrude","SWEPT_BODY",BODY,{"disambiguationData":[OSD([sQuery(id+"F15.wireOp",EDGE,"E46"),sQuery(id+"F15.wireOp",EDGE,"E47"),sQuery(id+"F15.wireOp",EDGE,"E48"),sQuery(id+"F15.wireOp",EDGE,"E49"),sQuery(id+"F15.wireOp",EDGE,"E50"),sQuery(id+"F15.wireOp",EDGE,"E53"),sQuery(id+"F15.wireOp",EDGE,"E54"),sQuery(id+"F15.wireOp",EDGE,"E55"),sQuery(id+"F15.wireOp",EDGE,"E56"),sQuery(id+"F15.wireOp",EDGE,"E57"),sQuery(id+"F15.wireOp",EDGE,"E58"),sQuery(id+"F15.wireOp",EDGE,"E59"),sQuery(id+"F15.wireOp",EDGE,"E60"),sQuery(id+"F15.wireOp",EDGE,"E61"),sQuery(id+"F15.wireOp",EDGE,"E62"),sQuery(id+"F15.wireOp",EDGE,"E63"),sQuery(id+"F15.wireOp",EDGE,"E64"),sQuery(id+"F15.wireOp",EDGE,"E65"),sQuery(id+"F15.wireOp",EDGE,"E85"),sQuery(id+"F15.wireOp",EDGE,"E86"),sQuery(id+"F15.wireOp",EDGE,"E88.filletArc"),sQuery(id+"F15.wireOp",EDGE,"E89.filletArc"),sQuery(id+"F15.wireOp",EDGE,"E90.filletArc"),sQuery(id+"F15.wireOp",EDGE,"E92.filletArc"),sQuery(id+"F15.wireOp",EDGE,"E93.filletArc")])]});
            var Q1;
            Q1=qCreatedBy(makeId("Right.planeOp"),FACE);
            mirror(context, id + "F28", {"entities" : qUnion([Q0]), "mirrorPlane" : qUnion([Q1])});
        }
        {
            var Q0;
            Q0=makeQuery(id+"F28.opPattern","COPY",BODY,{"derivedFrom":makeQuery(id+"F16.opExtrude","SWEPT_BODY",BODY,{"disambiguationData":[OSD([sQuery(id+"F15.wireOp",EDGE,"E46"),sQuery(id+"F15.wireOp",EDGE,"E47"),sQuery(id+"F15.wireOp",EDGE,"E48"),sQuery(id+"F15.wireOp",EDGE,"E49"),sQuery(id+"F15.wireOp",EDGE,"E50"),sQuery(id+"F15.wireOp",EDGE,"E53"),sQuery(id+"F15.wireOp",EDGE,"E54"),sQuery(id+"F15.wireOp",EDGE,"E55"),sQuery(id+"F15.wireOp",EDGE,"E56"),sQuery(id+"F15.wireOp",EDGE,"E57"),sQuery(id+"F15.wireOp",EDGE,"E58"),sQuery(id+"F15.wireOp",EDGE,"E59"),sQuery(id+"F15.wireOp",EDGE,"E60"),sQuery(id+"F15.wireOp",EDGE,"E61"),sQuery(id+"F15.wireOp",EDGE,"E62"),sQuery(id+"F15.wireOp",EDGE,"E63"),sQuery(id+"F15.wireOp",EDGE,"E64"),sQuery(id+"F15.wireOp",EDGE,"E65"),sQuery(id+"F15.wireOp",EDGE,"E85"),sQuery(id+"F15.wireOp",EDGE,"E86"),sQuery(id+"F15.wireOp",EDGE,"E88.filletArc"),sQuery(id+"F15.wireOp",EDGE,"E89.filletArc"),sQuery(id+"F15.wireOp",EDGE,"E90.filletArc"),sQuery(id+"F15.wireOp",EDGE,"E92.filletArc"),sQuery(id+"F15.wireOp",EDGE,"E93.filletArc")])]}),"instanceName":"1"});
            transform(context, id + "F29", {"entities" : qUnion([Q0]), "transformType" : TransformType.TRANSLATION_3D, "dx" : 0 * mm, "dy" : 0 * mm, "dz" : 500 * mm, "makeCopy" : false});
        }
        {
            var Q0;
            Q0=makeQuery(id+"F26.opExtrude","CAP_FACE",FACE,{"disambiguationData":[OSD([sQuery(id+"F25.wireOp",EDGE,"E173"),sQuery(id+"F25.wireOp",EDGE,"E174"),sQuery(id+"F25.wireOp",EDGE,"E175"),sQuery(id+"F25.wireOp",EDGE,"E176")])],"isStart":false});
            var sketch = newSketch(context, id + "F30", { "sketchPlane" : qUnion([Q0])});
            skPoint(sketch, "E181", {"position": v(48.66, -266.25) * mm});
            skPoint(sketch, "E182", {"position": v(238.66, -266.25) * mm});
            skPoint(sketch, "E183", {"position": v(143.66, -355.64) * mm});
            skCircle(sketch, "E184", {"center": v(143.66, -260.46) * mm, "radius": 95.18 * mm, "construction": true});
            skPoint(sketch, "E184.third.point", {"position": v(128.54, -354.43) * mm});
            skCircle(sketch, "E185", {"center": v(143.66, -260.46) * mm, "radius": 65 * mm});
            skCircle(sketch, "E186", {"center": v(143.66, -218.96) * mm, "radius": 12 * mm});
            skPoint(sketch, "E187", {"position": v(20.87, 30.54) * mm});
            skPoint(sketch, "E188", {"position": v(20.87, 72.04) * mm});
            skLineSegment(sketch, "E189", {"start": v(20.87, 30.54) * mm, "end": v(20.87, 72.04) * mm, "construction": true});
            skLineSegment(sketch, "E190", {"start": v(143.66, -260.46) * mm, "end": v(143.66, -218.96) * mm, "construction": true});
            skCircle(sketch, "E191.1.0", {"center": v(179.6, -239.7) * mm, "radius": 12 * mm});
            skCircle(sketch, "E191.2.0", {"center": v(179.6, -281.2) * mm, "radius": 12 * mm});
            skCircle(sketch, "E191.3.0", {"center": v(143.66, -301.96) * mm, "radius": 12 * mm});
            skCircle(sketch, "E191.4.0", {"center": v(107.72, -281.2) * mm, "radius": 12 * mm});
            skCircle(sketch, "E191.5.0", {"center": v(107.72, -239.7) * mm, "radius": 12 * mm});
            skLineSegment(sketch, "E191.anchor2", {"start": v(143.66, -260.46) * mm, "end": v(107.72, -239.7) * mm, "construction": true});
            skSolve(sketch);
        }
        {
            var Q0;
            Q0=makeQuery(id+"F30.imprint","IMPRINT",FACE,{"disambiguationData":[TD([[makeQuery(id+"F30.imprint","IMPRINT",EDGE,{"derivedFrom":sQuery(id+"F30.wireOp",EDGE,"E185")}),1.0]])]});
            extrude(context, id + "F31", {"entities" : qUnion([Q0]), "operationType" : NewBodyOperationType.ADD, "depth" : 5 * mm});
        }
        {
            var Q0;
            Q0=qCreatedBy(makeId("Right.planeOp"),FACE);
            var sketch = newSketch(context, id + "F32", { "sketchPlane" : qUnion([Q0])});
            skCircle(sketch, "E192", {"center": v(186.77, -54.98) * mm, "radius": 19.95 * mm});
            skCircle(sketch, "E193", {"center": v(186.77, -54.98) * mm, "radius": 2.5 * mm});
            skPoint(sketch, "E194", {"position": v(-266.99, 39.68) * mm});
            skPoint(sketch, "E195", {"position": v(-266.99, 52.63) * mm});
            skLineSegment(sketch, "E196", {"start": v(-266.99, 39.68) * mm, "end": v(-266.99, 52.63) * mm, "construction": true});
            skLineSegment(sketch, "E197", {"start": v(186.77, -54.98) * mm, "end": v(186.77, -42.03) * mm, "construction": true});
            skLineSegment(sketch, "E198", {"start": v(186.77, -42.03) * mm, "end": v(186.77, -35.03) * mm, "construction": true});
            skSolve(sketch);
        }
        {
            var Q0;
            Q0=makeQuery(id+"F32.imprint","IMPRINT",FACE,{"disambiguationData":[TD([[makeQuery(id+"F32.imprint","IMPRINT",EDGE,{"derivedFrom":sQuery(id+"F32.wireOp",EDGE,"E192")}),1.0]])]});
            extrude(context, id + "F33", {"entities" : qUnion([Q0]), "depth" : 120 * mm});
        }
        {
            var Q0;
            Q0=qCreatedBy(makeId("Front.planeOp"),FACE);
            var sketch = newSketch(context, id + "F34", { "sketchPlane" : qUnion([Q0])});
            skPoint(sketch, "E199", {"position": v(38.66, -75.46) * mm});
            skPoint(sketch, "E200", {"position": v(248.66, -75.46) * mm});
            skLineSegment(sketch, "E201", {"start": v(38.66, -75.46) * mm, "end": v(248.66, -75.46) * mm, "construction": true});
            skCircle(sketch, "E202", {"center": v(143.66, 189.08) * mm, "radius": 105 * mm, "construction": true});
            skPoint(sketch, "E203", {"position": v(143.66, -75.46) * mm});
            skPoint(sketch, "E204", {"position": v(248.66, 189.08) * mm});
            skArc(sketch, "E205", {"start": v(248.66, 189.08) * mm, "mid": v(143.66, 294.08) * mm, "end": v(38.66, 189.08) * mm});
            skArc(sketch, "E206", {"start": v(248.66, 109.08) * mm, "mid": v(143.66, 4.08) * mm, "end": v(38.66, 109.08) * mm});
            skLineSegment(sketch, "E207", {"start": v(248.66, 109.08) * mm, "end": v(248.66, 189.08) * mm});
            skLineSegment(sketch, "E208", {"start": v(38.66, 109.08) * mm, "end": v(38.66, 189.08) * mm});
            skPoint(sketch, "E209", {"position": v(143.5, -365.64) * mm});
            skPoint(sketch, "E210", {"position": v(143.66, -260.46) * mm});
            skPoint(sketch, "E211", {"position": v(143.66, 4.08) * mm});
            skLineSegment(sketch, "E212", {"start": v(143.66, -260.46) * mm, "end": v(143.5, -365.64) * mm, "construction": true});
            skLineSegment(sketch, "E213", {"start": v(143.66, 4.08) * mm, "end": v(143.66, 109.25) * mm, "construction": true});
            skCircle(sketch, "E214", {"center": v(143.66, 109.25) * mm, "radius": 65 * mm});
            skSolve(sketch);
        }
        {
            var Q0;
            Q0=makeQuery(id+"F34.imprint","IMPRINT",FACE,{"disambiguationData":[TD([[makeQuery(id+"F34.imprint","IMPRINT",EDGE,{"derivedFrom":sQuery(id+"F34.wireOp",EDGE,"E205")}),1.0]])]});
            extrude(context, id + "F35", {"entities" : qUnion([Q0]), "depth" : 320 * mm});
        }
        {
            var Q0;
            Q0=qCreatedBy(makeId("Front.planeOp"),FACE);
            var sketch = newSketch(context, id + "F36", { "sketchPlane" : qUnion([Q0])});
            skPoint(sketch, "E215", {"position": v(143.66, -260.46) * mm});
            skPoint(sketch, "E216", {"position": v(143.66, -325.46) * mm});
            skCircle(sketch, "E217", {"center": v(-292.15, -260.46) * mm, "radius": 65 * mm, "construction": true});
            skLineSegment(sketch, "E218", {"start": v(143.66, -260.46) * mm, "end": v(143.66, -325.46) * mm, "construction": true});
            skLineSegment(sketch, "E219", {"start": v(-292.15, -260.46) * mm, "end": v(-292.15, -325.46) * mm, "construction": true});
            skLineSegment(sketch, "E220", {"start": v(-187.15, -260.46) * mm, "end": v(-397.15, -260.46) * mm, "construction": true});
            skCircle(sketch, "E221", {"center": v(-292.15, -260.46) * mm, "radius": 105 * mm, "construction": true});
            skPoint(sketch, "E221.second.point", {"position": v(-310.04, -157) * mm});
            skCircle(sketch, "E222", {"center": v(-292.15, -260.46) * mm, "radius": 105 * mm});
            skPoint(sketch, "E223", {"position": v(248.66, 189.08) * mm});
            skPoint(sketch, "E224", {"position": v(38.66, 189.08) * mm});
            skLineSegment(sketch, "E225", {"start": v(248.66, 189.08) * mm, "end": v(38.66, 189.08) * mm, "construction": true});
            skSolve(sketch);
        }
        {
            var Q0;
            Q0=makeQuery(id+"F36.imprint","IMPRINT",FACE,{"disambiguationData":[TD([[makeQuery(id+"F36.imprint","IMPRINT",EDGE,{"derivedFrom":sQuery(id+"F36.wireOp",EDGE,"E222")}),1.0]])]});
            extrude(context, id + "F37", {"entities" : qUnion([Q0]), "depth" : 10 * mm});
        }
        {
            var Q0;
            Q0=makeQuery(id+"F37.opExtrude","CAP_FACE",FACE,{"disambiguationData":[OSD([sQuery(id+"F36.wireOp",EDGE,"E222")])],"isStart":true});
            var sketch = newSketch(context, id + "F38", { "sketchPlane" : qUnion([Q0])});
            skPoint(sketch, "E226", {"position": v(499.31, -258.82) * mm});
            skPoint(sketch, "E227", {"position": v(499.31, -288.59) * mm});
            skCircle(sketch, "E228", {"center": v(205.62, -258.82) * mm, "radius": 29.76 * mm, "construction": true});
            skLineSegment(sketch, "E229", {"start": v(499.31, -258.82) * mm, "end": v(499.31, -288.59) * mm, "construction": true});
            skLineSegment(sketch, "E230", {"start": v(205.62, -258.82) * mm, "end": v(205.62, -288.59) * mm, "construction": true});
            skLineSegment(sketch, "E231", {"start": v(548.07, -263.06) * mm, "end": v(450.56, -263.06) * mm, "construction": true});
            skLineSegment(sketch, "E232", {"start": v(254.38, -258.82) * mm, "end": v(156.86, -258.82) * mm, "construction": true});
            skCircle(sketch, "E233", {"center": v(205.62, -258.82) * mm, "radius": 48.76 * mm, "construction": true});
            skPoint(sketch, "E233.second.point", {"position": v(197.31, -210.78) * mm});
            skCircle(sketch, "E234", {"center": v(292.15, -260.46) * mm, "radius": 29.76 * mm, "construction": true});
            skCircle(sketch, "E235", {"center": v(292.15, -260.46) * mm, "radius": 100 * mm});
            skSolve(sketch);
        }
        {
            var Q0;
            Q0=makeQuery(id+"F38.imprint","IMPRINT",FACE,{"disambiguationData":[TD([[makeQuery(id+"F38.imprint","IMPRINT",EDGE,{"derivedFrom":sQuery(id+"F38.wireOp",EDGE,"E235")}),1.0]])]});
            extrude(context, id + "F39", {"entities" : qUnion([Q0]), "operationType" : NewBodyOperationType.ADD, "depth" : 35 * mm});
        }
        {
            var Q0;
            Q0=makeQuery(id+"F39.opExtrude","CAP_FACE",FACE,{"disambiguationData":[OSD([sQuery(id+"F38.wireOp",EDGE,"E235")])],"isStart":false});
            var sketch = newSketch(context, id + "F40", { "sketchPlane" : qUnion([Q0])});
            skCircle(sketch, "E236", {"center": v(292.15, -260.46) * mm, "radius": 75 * mm});
            skCircle(sketch, "E237", {"center": v(292.15, -260.46) * mm, "radius": 65 * mm, "construction": true});
            skSolve(sketch);
        }
        {
            var Q0;
            Q0=makeQuery(id+"F40.imprint","IMPRINT",FACE,{"disambiguationData":[TD([[makeQuery(id+"F40.imprint","IMPRINT",EDGE,{"derivedFrom":sQuery(id+"F40.wireOp",EDGE,"E236")}),1.0]])]});
            extrude(context, id + "F41", {"entities" : qUnion([Q0]), "operationType" : NewBodyOperationType.ADD, "depth" : 30 * mm});
        }
        {
            var Q0;
            Q0=makeQuery(id+"F41.opExtrude","CAP_FACE",FACE,{"disambiguationData":[OSD([sQuery(id+"F40.wireOp",EDGE,"E236")])],"isStart":false});
            var sketch = newSketch(context, id + "F42", { "sketchPlane" : qUnion([Q0])});
            skCircle(sketch, "E238", {"center": v(292.15, -260.46) * mm, "radius": 93 * mm});
            skCircle(sketch, "E239", {"center": v(292.15, -260.46) * mm, "radius": 75 * mm, "construction": true});
            skSolve(sketch);
        }
        {
            var Q0;
            Q0=makeQuery(id+"F42.imprint","IMPRINT",FACE,{"disambiguationData":[TD([[makeQuery(id+"F42.imprint","IMPRINT",EDGE,{"derivedFrom":makeQuery(id+"F41.opExtrude","CAP_EDGE",EDGE,{"disambiguationData":[OSD([sQuery(id+"F40.wireOp",EDGE,"E236")])],"isStart":false})}),1.0]])]});
            var Q1;
            Q1=makeQuery(id+"F42.imprint","IMPRINT",FACE,{"disambiguationData":[TD([[makeQuery(id+"F42.imprint","IMPRINT",EDGE,{"derivedFrom":sQuery(id+"F42.wireOp",EDGE,"E238")}),1.0]])]});
            extrude(context, id + "F43", {"entities" : qUnion([Q0, Q1]), "operationType" : NewBodyOperationType.ADD, "depth" : 35 * mm});
        }
        {
            var Q0;
            Q0=makeQuery(id+"F43.opExtrude","CAP_FACE",FACE,{"disambiguationData":[OSD([sQuery(id+"F42.wireOp",EDGE,"E238")])],"isStart":false});
            var sketch = newSketch(context, id + "F44", { "sketchPlane" : qUnion([Q0])});
            skCircle(sketch, "E240", {"center": v(292.15, -260.46) * mm, "radius": 75 * mm});
            skSolve(sketch);
        }
        {
            var Q0;
            Q0=makeQuery(id+"F44.imprint","IMPRINT",FACE,{"disambiguationData":[TD([[makeQuery(id+"F44.imprint","IMPRINT",EDGE,{"derivedFrom":sQuery(id+"F44.wireOp",EDGE,"E240")}),1.0]])]});
            extrude(context, id + "F45", {"entities" : qUnion([Q0]), "operationType" : NewBodyOperationType.ADD, "depth" : 30 * mm});
        }
        {
            var Q0;
            Q0=makeQuery(id+"F39.opExtrude","CAP_EDGE",EDGE,{"disambiguationData":[OSD([sQuery(id+"F38.wireOp",EDGE,"E235")])],"isStart":false});
            var Q1;
            Q1=makeQuery(id+"F43.opExtrude","CAP_EDGE",EDGE,{"disambiguationData":[OSD([sQuery(id+"F42.wireOp",EDGE,"E238")])],"isStart":true});
            var Q2;
            Q2=makeQuery(id+"F43.opExtrude","CAP_EDGE",EDGE,{"disambiguationData":[OSD([sQuery(id+"F42.wireOp",EDGE,"E238")])],"isStart":false});
            var Q3;
            Q3=makeQuery(id+"F37.opExtrude","CAP_EDGE",EDGE,{"disambiguationData":[OSD([sQuery(id+"F36.wireOp",EDGE,"E222")])],"isStart":true});
            fillet(context, id + "F46", {"entities" : qUnion([Q0, Q1, Q2, Q3]), "radius" : 5 * mm, "rho" : 0.5, "crossSection" : FilletCrossSection.CONIC, "allowEdgeOverflow" : false});
        }
        {
            var Q0;
            Q0=makeQuery(id+"F46.opFillet","BLEND_EDGE",EDGE,{"blendedFrom":[makeQuery(id+"F37.opExtrude","CAP_EDGE",EDGE,{"disambiguationData":[OSD([sQuery(id+"F36.wireOp",EDGE,"E222")])],"isStart":true}),makeQuery(id+"F39.opExtrude","SWEPT_FACE",FACE,{"disambiguationData":[OSD([sQuery(id+"F38.wireOp",EDGE,"E235")])]})],"blendedInto":[makeQuery(id+"F39.opExtrude","SWEPT_FACE",FACE,{"disambiguationData":[OSD([sQuery(id+"F38.wireOp",EDGE,"E235")])]})]});
            var Q1;
            Q1=makeQuery(id+"F41.opExtrude","CAP_EDGE",EDGE,{"disambiguationData":[OSD([sQuery(id+"F40.wireOp",EDGE,"E236")])],"isStart":true});
            var Q2;
            Q2=makeQuery(id+"F45.opExtrude","CAP_EDGE",EDGE,{"disambiguationData":[OSD([sQuery(id+"F44.wireOp",EDGE,"E240")])],"isStart":true});
            var Q3;
            Q3=makeQuery(id+"F41.opExtrude","CAP_EDGE",EDGE,{"disambiguationData":[OSD([sQuery(id+"F40.wireOp",EDGE,"E236")])],"isStart":false});
            fillet(context, id + "F47", {"entities" : qUnion([Q0, Q1, Q2, Q3]), "radius" : 1 * mm, "tangentPropagation" : true, "allowEdgeOverflow" : false});
        }
    });
